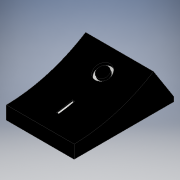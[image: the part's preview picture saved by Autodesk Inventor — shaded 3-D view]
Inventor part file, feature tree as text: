
AUTODESK INVENTOR PART (.ipt)
format: ipt  version: 2019 (Build 230136000, 136)  size: 137,216 bytes
history: native  units: in
note: dims shown in document units (in); Inventor stores cm internally (conversion verified against a paired STEP export)
features: other x7, extrude x3, sketch x3
ambient origin geometry x8: Origin, YZ Plane, XZ Plane, XY Plane, X Axis, Y Axis, Z Axis, Center Point
bodies: Solid1 (feature_tree)
feature tree (13):
  extrude  "Extrusion1"  Depth=0.03in TaperAngle=0.0deg
  extrude  "Extrusion2"  TaperAngle=0.0deg  [1 undecoded]
  extrude  "Extrusion3"  [1 undecoded]
  other  "to_body_XY"
  other  "to_body_YZ"
  other  "to_body_ZX"
  other  "to_body_X"
  other  "to_body_Y"
  other  "to_body_Z"
  other  "to_body_Center"
  sketch  "Sketch_2"  dims[d0=0.417in d1=0.0in d2=0.03in d3=0.0in]
  sketch  "Sketch_3"  dims[d4=0.03in d5=0.0in d6=0.0in]
  sketch  "Sketch_4"
note: 2 required parameter values undecoded (feature->parameter linkage not recoverable at this tier; creation-order binding heuristic only, values carry confidence <= 0.55)
